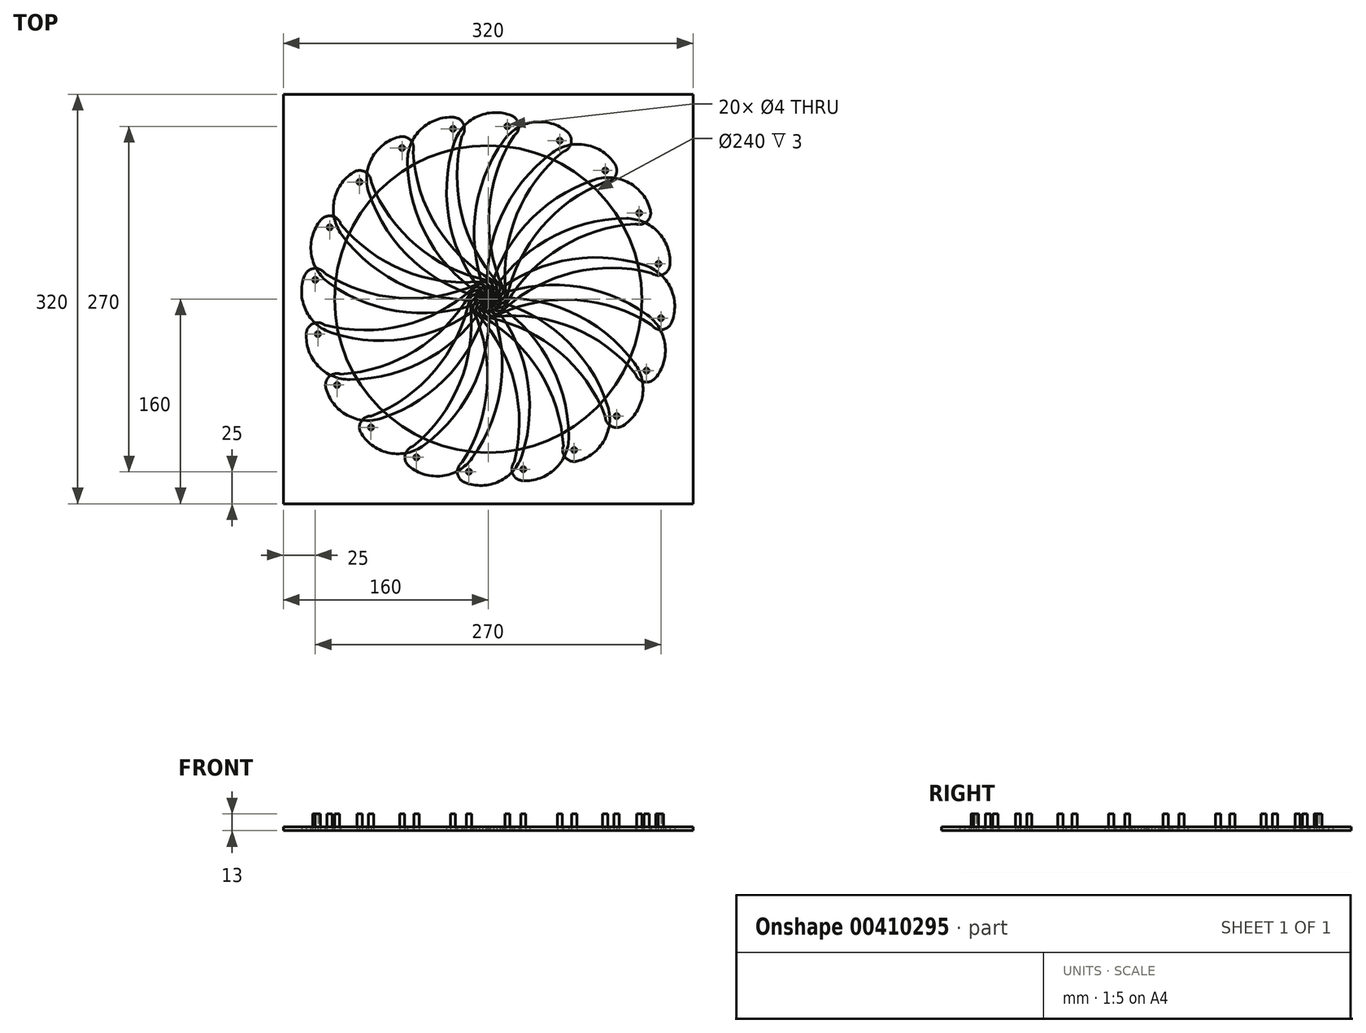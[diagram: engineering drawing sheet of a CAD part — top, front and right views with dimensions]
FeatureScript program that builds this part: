
annotation { "Feature Type Name" : "Feature", "Feature Type Description" : "" }
export const myFeature = defineFeature(function(context is Context, id is Id, definition is map)
    precondition{}
    {
        {
            var Q0;
            Q0=qCreatedBy(makeId("Top.planeOp"),FACE);
            var sketch = newSketch(context, id + "F0", { "sketchPlane" : qUnion([Q0])});
            skCircle(sketch, "E0", {"center": v(0, 0) * mm, "radius": 120 * mm});
            skLineSegment(sketch, "E1", {"start": v(0, 43.02) * mm, "end": v(0, -45.8) * mm, "construction": true});
            skLineSegment(sketch, "E2", {"start": v(-53.33, 0) * mm, "end": v(48.3, 0) * mm, "construction": true});
            skLineSegment(sketch, "E3.bottom", {"start": v(-160, 160) * mm, "end": v(160, 160) * mm});
            skLineSegment(sketch, "E3.top", {"start": v(-160, -160) * mm, "end": v(160, -160) * mm});
            skLineSegment(sketch, "E3.left", {"start": v(-160, 160) * mm, "end": v(-160, -160) * mm});
            skLineSegment(sketch, "E3.right", {"start": v(160, 160) * mm, "end": v(160, -160) * mm});
            skSolve(sketch);
        }
        {
            var Q0;
            Q0=makeQuery(id+"F0.imprint","IMPRINT",FACE,{"disambiguationData":[TD([[makeQuery(id+"F0.imprint","IMPRINT",EDGE,{"derivedFrom":sQuery(id+"F0.wireOp",EDGE,"E0")}),-1.0]])]});
            extrude(context, id + "F1", {"entities" : qUnion([Q0]), "depth" : 3 * mm});
        }
        {
            var Q0;
            Q0=makeQuery(id+"F1.opExtrude","CAP_FACE",FACE,{"disambiguationData":[OSD([sQuery(id+"F0.wireOp",EDGE,"E0"),sQuery(id+"F0.wireOp",EDGE,"E3.bottom"),sQuery(id+"F0.wireOp",EDGE,"E3.top"),sQuery(id+"F0.wireOp",EDGE,"E3.left"),sQuery(id+"F0.wireOp",EDGE,"E3.right")])],"isStart":false});
            var sketch = newSketch(context, id + "F2", { "sketchPlane" : qUnion([Q0])});
            skCircle(sketch, "E4", {"center": v(15, 135) * mm, "radius": 2 * mm});
            skCircle(sketch, "E5.1.0", {"center": v(-27.45, 133.03) * mm, "radius": 2 * mm});
            skCircle(sketch, "E5.2.0", {"center": v(-67.22, 118.03) * mm, "radius": 2 * mm});
            skCircle(sketch, "E5.3.0", {"center": v(-100.4, 91.49) * mm, "radius": 2 * mm});
            skCircle(sketch, "E5.4.0", {"center": v(-123.76, 55.98) * mm, "radius": 2 * mm});
            skCircle(sketch, "E5.5.0", {"center": v(-135, 15) * mm, "radius": 2 * mm});
            skCircle(sketch, "E5.6.0", {"center": v(-133.03, -27.45) * mm, "radius": 2 * mm});
            skCircle(sketch, "E5.7.0", {"center": v(-118.03, -67.22) * mm, "radius": 2 * mm});
            skCircle(sketch, "E5.8.0", {"center": v(-91.49, -100.4) * mm, "radius": 2 * mm});
            skCircle(sketch, "E5.9.0", {"center": v(-55.98, -123.76) * mm, "radius": 2 * mm});
            skCircle(sketch, "E5.10.0", {"center": v(-15, -135) * mm, "radius": 2 * mm});
            skCircle(sketch, "E5.11.0", {"center": v(27.45, -133.03) * mm, "radius": 2 * mm});
            skCircle(sketch, "E5.12.0", {"center": v(67.22, -118.03) * mm, "radius": 2 * mm});
            skCircle(sketch, "E5.13.0", {"center": v(100.4, -91.49) * mm, "radius": 2 * mm});
            skCircle(sketch, "E5.14.0", {"center": v(123.76, -55.98) * mm, "radius": 2 * mm});
            skPoint(sketch, "E5.center", {"position": v(0, 0) * mm});
            skCircle(sketch, "E6.1.15.0", {"center": v(135, -15) * mm, "radius": 2 * mm});
            skCircle(sketch, "E6.1.16.0", {"center": v(133.03, 27.45) * mm, "radius": 2 * mm});
            skCircle(sketch, "E6.1.17.0", {"center": v(118.03, 67.22) * mm, "radius": 2 * mm});
            skCircle(sketch, "E6.1.18.0", {"center": v(91.49, 100.4) * mm, "radius": 2 * mm});
            skCircle(sketch, "E6.1.19.0", {"center": v(55.98, 123.76) * mm, "radius": 2 * mm});
            skSolve(sketch);
        }
        {
            var Q0;
            Q0 = qSketchRegion(id + "F2", true);
            extrude(context, id + "F3", {"entities" : qUnion([Q0]), "operationType" : NewBodyOperationType.ADD, "depth" : 10 * mm});
        }
        {
            var Q0;
            Q0=qCreatedBy(makeId("Top.planeOp"),FACE);
            var sketch = newSketch(context, id + "F4", { "sketchPlane" : qUnion([Q0])});
            skCircle(sketch, "E7", {"center": v(0, 0) * mm, "radius": 125 * mm, "construction": true});
            skArc(sketch, "E8", {"start": v(-26.52, 122.16) * mm, "mid": v(-29.62, 57.52) * mm, "end": v(0, 0) * mm});
            skCircle(sketch, "E9.0", {"center": v(15, 135) * mm, "radius": 2 * mm});
            skArc(sketch, "E10", {"start": v(20.05, 127.55) * mm, "mid": v(0.84, 69.8) * mm, "end": v(11.17, 9.83) * mm});
            skLineSegment(sketch, "E11", {"start": v(0, 0) * mm, "end": v(4.77, 0) * mm});
            skPoint(sketch, "E12.visualSharp", {"position": v(16.05, 0) * mm});
            skArc(sketch, "E12.filletArc", {"start": v(4.77, 0) * mm, "mid": v(10.64, 3.18) * mm, "end": v(11.17, 9.83) * mm});
            skArc(sketch, "E13", {"start": v(20.05, 127.55) * mm, "mid": v(23.95, 135.99) * mm, "end": v(18.3, 143.37) * mm});
            skArc(sketch, "E14", {"start": v(18.3, 143.37) * mm, "mid": v(-8.72, 142.47) * mm, "end": v(-26.53, 122.11) * mm});
            skSolve(sketch);
        }
        {
            var Q0;
            {var subQ2=sQuery(id+"F4.wireOp",EDGE,"E8");Q0=makeQuery(id+"F4.imprint","IMPRINT",FACE,{"disambiguationData":[TD([[makeQuery(id+"F4.imprint","IMPRINT",EDGE,{"derivedFrom":subQ2}),1.0]])]});}
            extrude(context, id + "F5", {"entities" : qUnion([Q0]), "depth" : 3 * mm});
        }
        {
            var Q0;
            Q0=makeQuery(id+"F5.opExtrude","SWEPT_BODY",BODY,{"disambiguationData":[OSD([sQuery(id+"F4.wireOp",EDGE,"E8"),sQuery(id+"F4.wireOp",EDGE,"2d515107-7a83-4378-ba64-e586f5fe6628.14.0"),sQuery(id+"F4.wireOp",EDGE,"daqgzb58-1Qsf-domH-fy6u-O6Z0h6G8pY7R"),sQuery(id+"F4.wireOp",EDGE,"881e4rIN-yicR-qTvN-inSL-3wopSEfX8S8y"),sQuery(id+"F4.wireOp",EDGE,"E9.0")])]});
            var Q1;
            Q1=makeQuery(id+"F1.opExtrude","CAP_EDGE",EDGE,{"disambiguationData":[OSD([sQuery(id+"F0.wireOp",EDGE,"E0")])],"isStart":false});
            circularPattern(context, id + "F6", {"entities" : qUnion([Q0]), "axis" : qUnion([Q1]), "angle" : 360 * degree, "instanceCount" : 20, "oppositeDirection" : true, "equalSpace" : true});
        }
    });
